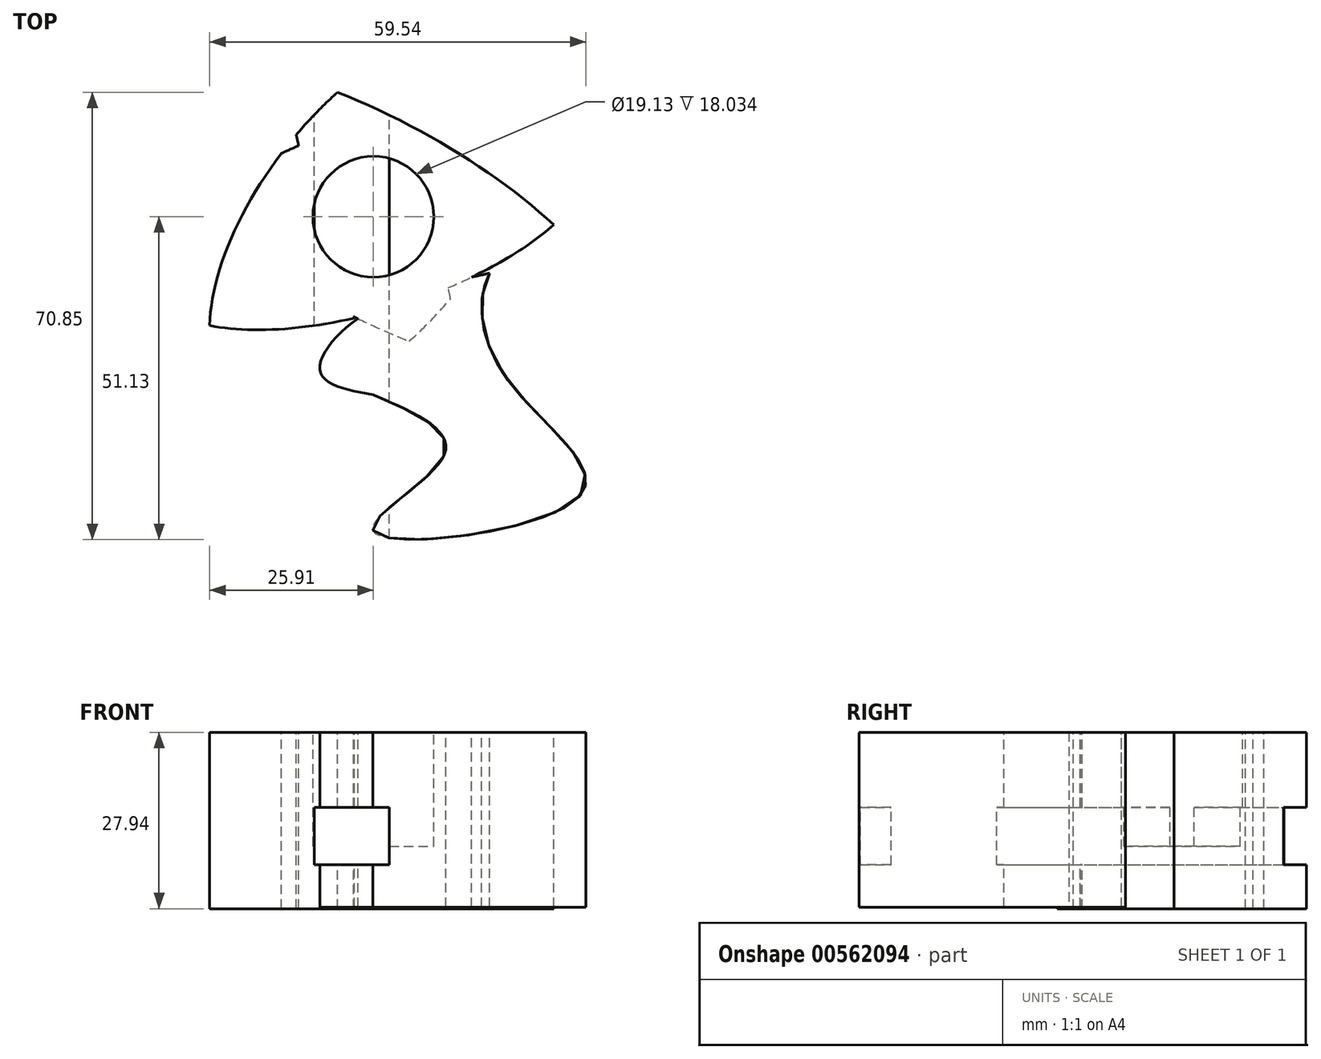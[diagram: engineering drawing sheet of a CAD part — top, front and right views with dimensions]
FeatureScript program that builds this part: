
annotation { "Feature Type Name" : "Feature", "Feature Type Description" : "" }
export const myFeature = defineFeature(function(context is Context, id is Id, definition is map)
    precondition{}
    {
        {
            var Q0;
            Q0=qCreatedBy(makeId("Top.planeOp"),FACE);
            var sketch = newSketch(context, id + "F0", { "sketchPlane" : qUnion([Q0])});
            skEllipse(sketch, "E0", {"center": v(0, 0) * mm, "majorRadius": 43.92 * mm, "minorRadius": 15.46 * mm, "majorAxis": v(-0.88, 0.48)});
            skEllipse(sketch, "E1", {"center": v(0, 0) * mm, "majorRadius": 35.47 * mm, "minorRadius": 17.67 * mm, "majorAxis": v(0.62, 0.79)});
            skEllipse(sketch, "E2", {"center": v(0, 0) * mm, "majorRadius": 39.32 * mm, "minorRadius": 8.37 * mm, "majorAxis": v(0.3, -0.95)});
            skEllipse(sketch, "E3", {"center": v(0, 0) * mm, "majorRadius": 36.59 * mm, "minorRadius": 14.67 * mm, "majorAxis": v(0.95, 0.3)});
            skSolve(sketch);
        }
        {
            var Q0;
            {var subQ0=sQuery(id+"F0.wireOp",EDGE,"E2");var subQ1=sQuery(id+"F0.wireOp",EDGE,"E0");var subQ6=makeQuery(id+"F0.imprint","INTERSECT",VERTEX,{"disambiguationData":[OD(2.0)],"derivedFrom":[subQ1,subQ0]});Q0=makeQuery(id+"F0.imprint","IMPRINT",FACE,{"disambiguationData":[TD([[makeQuery(id+"F0.imprint","IMPRINT",EDGE,{"disambiguationData":[TD([[subQ6,-1.0]])],"derivedFrom":subQ1}),1.0]])]});}
            var Q1;
            {var subQ0=sQuery(id+"F0.wireOp",EDGE,"E1");var subQ1=sQuery(id+"F0.wireOp",EDGE,"E0");var subQ2=makeQuery(id+"F0.imprint","INTERSECT",VERTEX,{"disambiguationData":[OD(2.0)],"derivedFrom":[subQ1,subQ0]});Q1=makeQuery(id+"F0.imprint","IMPRINT",FACE,{"disambiguationData":[TD([[makeQuery(id+"F0.imprint","IMPRINT",EDGE,{"disambiguationData":[TD([[subQ2,-1.0]])],"derivedFrom":subQ1}),1.0]])]});}
            var Q2;
            {var subQ0=sQuery(id+"F0.wireOp",EDGE,"E1");var subQ1=sQuery(id+"F0.wireOp",EDGE,"E0");var subQ2=makeQuery(id+"F0.imprint","INTERSECT",VERTEX,{"disambiguationData":[OD(0.0)],"derivedFrom":[subQ1,subQ0]});Q2=makeQuery(id+"F0.imprint","IMPRINT",FACE,{"disambiguationData":[TD([[makeQuery(id+"F0.imprint","IMPRINT",EDGE,{"disambiguationData":[TD([[subQ2,-1.0]])],"derivedFrom":subQ1}),1.0]])]});}
            var Q3;
            {var subQ0=sQuery(id+"F0.wireOp",EDGE,"E3");var subQ1=sQuery(id+"F0.wireOp",EDGE,"E0");var subQ2=makeQuery(id+"F0.imprint","INTERSECT",VERTEX,{"disambiguationData":[OD(2.0)],"derivedFrom":[subQ1,subQ0]});Q3=makeQuery(id+"F0.imprint","IMPRINT",FACE,{"disambiguationData":[TD([[makeQuery(id+"F0.imprint","IMPRINT",EDGE,{"disambiguationData":[TD([[subQ2,-1.0]])],"derivedFrom":subQ1}),1.0]])]});}
            var Q4;
            {var subQ0=sQuery(id+"F0.wireOp",EDGE,"E3");var subQ1=sQuery(id+"F0.wireOp",EDGE,"E0");var subQ2=makeQuery(id+"F0.imprint","INTERSECT",VERTEX,{"disambiguationData":[OD(3.0)],"derivedFrom":[subQ1,subQ0]});Q4=makeQuery(id+"F0.imprint","IMPRINT",FACE,{"disambiguationData":[TD([[makeQuery(id+"F0.imprint","IMPRINT",EDGE,{"disambiguationData":[TD([[subQ2,-1.0]])],"derivedFrom":subQ1}),1.0]])]});}
            var Q5;
            {var subQ0=sQuery(id+"F0.wireOp",EDGE,"E3");var subQ1=sQuery(id+"F0.wireOp",EDGE,"E0");var subQ2=makeQuery(id+"F0.imprint","INTERSECT",VERTEX,{"disambiguationData":[OD(1.0)],"derivedFrom":[subQ1,subQ0]});Q5=makeQuery(id+"F0.imprint","IMPRINT",FACE,{"disambiguationData":[TD([[makeQuery(id+"F0.imprint","IMPRINT",EDGE,{"disambiguationData":[TD([[subQ2,-1.0]])],"derivedFrom":subQ1}),1.0]])]});}
            var Q6;
            {var subQ0=sQuery(id+"F0.wireOp",EDGE,"E1");var subQ1=sQuery(id+"F0.wireOp",EDGE,"E0");var subQ2=makeQuery(id+"F0.imprint","INTERSECT",VERTEX,{"disambiguationData":[OD(0.0)],"derivedFrom":[subQ1,subQ0]});Q6=makeQuery(id+"F0.imprint","IMPRINT",FACE,{"disambiguationData":[TD([[makeQuery(id+"F0.imprint","IMPRINT",EDGE,{"disambiguationData":[TD([[subQ2,-1.0]])],"derivedFrom":subQ1}),-1.0]])]});}
            extrude(context, id + "F1", {"entities" : qUnion([Q0, Q1, Q2, Q3, Q4, Q5, Q6]), "oppositeDirection" : true, "depth" : 27.94 * mm, "offsetDistance" : 25.4 * mm});
        }
        {
            var Q0;
            Q0=qCreatedBy(makeId("Top.planeOp"),FACE);
            var sketch = newSketch(context, id + "F2", { "sketchPlane" : qUnion([Q0])});
            skFitSpline(sketch, "E4", {"points": [v(0, -28.2) * mm, v(11.22, -37.7) * mm, v(0, -49.8) * mm, v(32.8, -44.03) * mm, v(21.3, -25.9) * mm, v(18.42, -8.92) * mm, v(27.63, -2.3) * mm], "startDerivative": vector(129.93, -55.85) * mm, "endDerivative": vector(84.81, 37.88) * mm});
            skFitSpline(sketch, "E5", {"points": [v(0, -28.2) * mm, v(-8.35, -24.75) * mm, v(-2.88, -16.4) * mm, v(18.42, -8.92) * mm], "startDerivative": vector(-41.42, 7.76) * mm, "endDerivative": vector(54.44, 12.18) * mm});
            skSolve(sketch);
        }
        {
            var Q0;
            Q0 = qSketchRegion(id + "F2", true);
            extrude(context, id + "F3", {"entities" : qUnion([Q0]), "operationType" : NewBodyOperationType.ADD, "oppositeDirection" : true, "depth" : 27.7 * mm, "offsetDistance" : 25.4 * mm});
        }
        {
            var Q0;
            Q0=qCreatedBy(makeId("Top.planeOp"),FACE);
            var sketch = newSketch(context, id + "F4", { "sketchPlane" : qUnion([Q0])});
            skCircle(sketch, "E6", {"center": v(0, 0) * mm, "radius": 9.57 * mm});
            skSolve(sketch);
        }
        {
            var Q0;
            Q0 = qSketchRegion(id + "F4", true);
            extrude(context, id + "F5", {"entities" : qUnion([Q0]), "operationType" : NewBodyOperationType.REMOVE, "oppositeDirection" : true, "depth" : 18.03 * mm, "offsetDistance" : 25.4 * mm});
        }
        {
            var Q0;
            Q0=qCreatedBy(makeId("Front.planeOp"),FACE);
            var sketch = newSketch(context, id + "F6", { "sketchPlane" : qUnion([Q0])});
            skLineSegment(sketch, "E7.bottom", {"start": v(-9.38, -21) * mm, "end": v(2.52, -21) * mm});
            skLineSegment(sketch, "E7.top", {"start": v(-9.38, -11.89) * mm, "end": v(2.52, -11.89) * mm});
            skLineSegment(sketch, "E7.left", {"start": v(-9.38, -21) * mm, "end": v(-9.38, -11.89) * mm});
            skLineSegment(sketch, "E7.right", {"start": v(2.52, -21) * mm, "end": v(2.52, -11.89) * mm});
            skSolve(sketch);
        }
        {
            var Q0;
            Q0 = qSketchRegion(id + "F6", true);
            extrude(context, id + "F7", {"entities" : qUnion([Q0]), "operationType" : NewBodyOperationType.REMOVE, "endBound" : BoundingType.SYMMETRIC, "depth" : 151.38 * mm, "offsetDistance" : 25.4 * mm});
        }
    });
